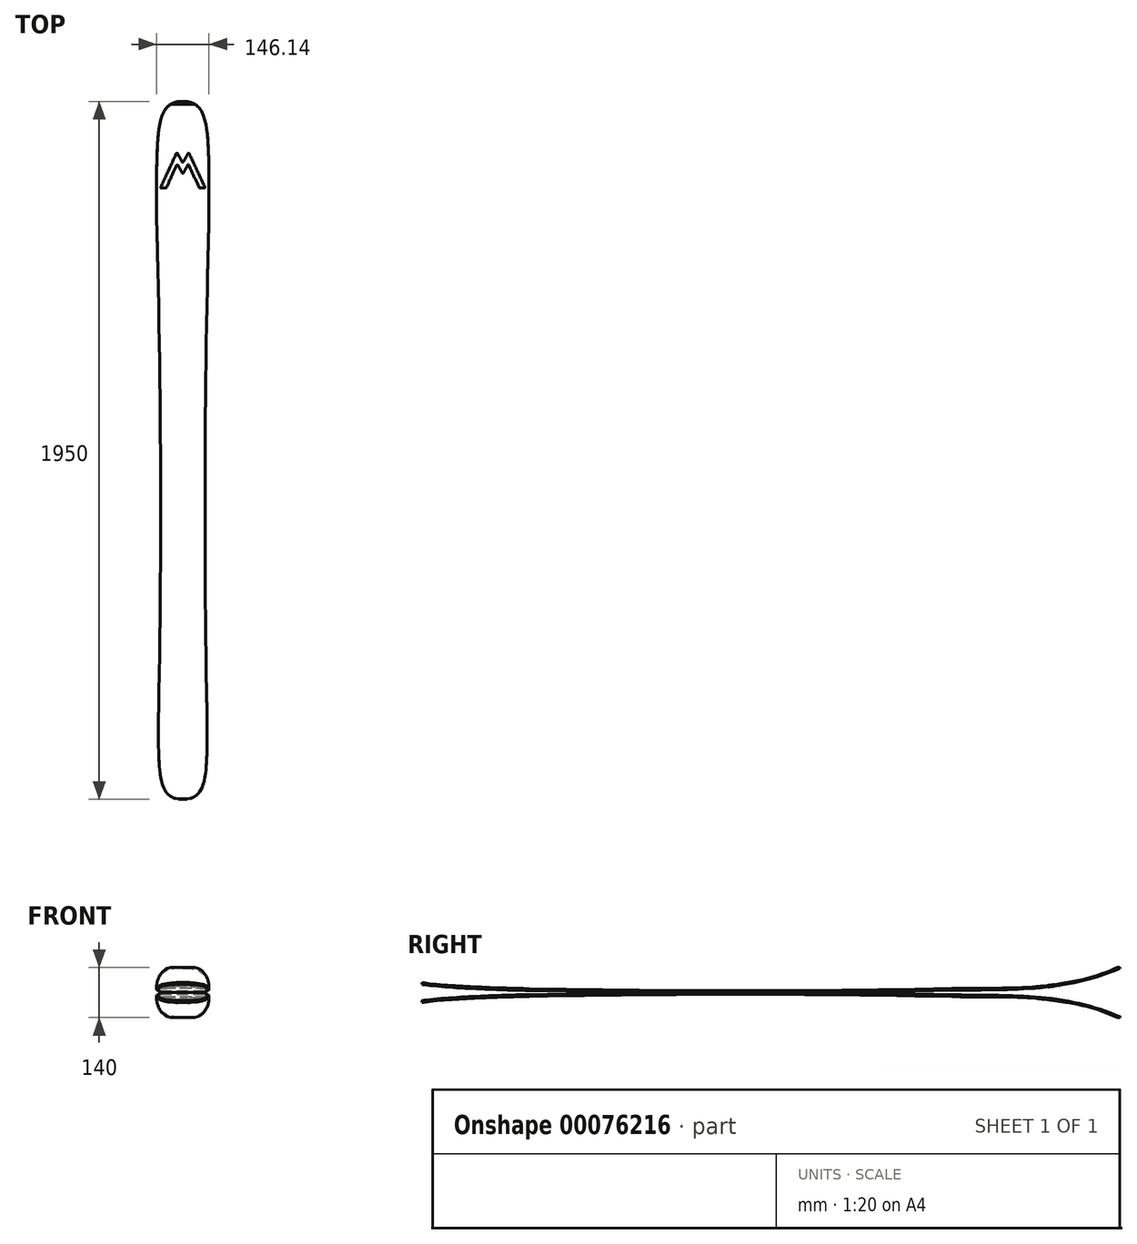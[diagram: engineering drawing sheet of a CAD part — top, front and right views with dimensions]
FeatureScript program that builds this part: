
annotation { "Feature Type Name" : "Feature", "Feature Type Description" : "" }
export const myFeature = defineFeature(function(context is Context, id is Id, definition is map)
    precondition{}
    {
        {
            var Q0;
            Q0=qCreatedBy(makeId("Right.planeOp"),FACE);
            var sketch = newSketch(context, id + "F0", { "sketchPlane" : qUnion([Q0])});
            skLineSegment(sketch, "E0", {"start": v(0, 23) * mm, "end": v(0, 0) * mm, "construction": true});
            skLineSegment(sketch, "E1", {"start": v(0, 0) * mm, "end": v(1950, 0) * mm, "construction": true});
            skLineSegment(sketch, "E2", {"start": v(1950, 0) * mm, "end": v(1950, 68) * mm, "construction": true});
            skLineSegment(sketch, "E3", {"start": v(880, 0) * mm, "end": v(880, 154.89) * mm, "construction": true});
            skLineSegment(sketch, "E4", {"start": v(300, 0) * mm, "end": v(300, 116.2) * mm, "construction": true});
            skLineSegment(sketch, "E5.MirrorCS", {"start": v(1480, 0) * mm, "end": v(1480, 116.2) * mm, "construction": true});
            skArc(sketch, "E6", {"start": v(300, 5.8) * mm, "mid": v(890, 0) * mm, "end": v(1480, 6.2) * mm});
            skFitSpline(sketch, "E7", {"points": [v(1480, 6.2) * mm, v(1950, 68) * mm], "startDerivative": vector(530.97, 10.99) * mm, "endDerivative": vector(480, 204) * mm});
            skFitSpline(sketch, "E8", {"points": [v(0, 23) * mm, v(300, 5.8) * mm], "startDerivative": vector(164.4, -29.03) * mm, "endDerivative": vector(280.54, -5.61) * mm});
            skFitSpline(sketch, "E9.0", {"points": [v(1479.9, 11.2) * mm, v(1524.2, 12.12) * mm, v(1607.23, 12.26) * mm, v(1702.48, 15.35) * mm, v(1776.9, 23.8) * mm, v(1851.28, 37.66) * mm, v(1908.31, 55.72) * mm, v(1948.04, 72.6) * mm]});
            skArc(sketch, "E9.1", {"start": v(300.1, 10.8) * mm, "mid": v(890, 5) * mm, "end": v(1479.9, 11.2) * mm});
            skFitSpline(sketch, "E9.2", {"points": [v(0.87, 27.92) * mm, v(4.22, 27.33) * mm, v(11.7, 26.17) * mm, v(29.49, 23.96) * mm, v(56.34, 21.42) * mm, v(94.05, 18.73) * mm, v(135.43, 16.4) * mm, v(178.64, 14.45) * mm, v(236.25, 12.32) * mm, v(276.74, 11.27) * mm, v(300.1, 10.8) * mm]});
            skLineSegment(sketch, "E10", {"start": v(0.87, 27.92) * mm, "end": v(0, 23) * mm});
            skLineSegment(sketch, "E11", {"start": v(1947.68, 72.45) * mm, "end": v(1950, 68) * mm});
            skSolve(sketch);
        }
        {
            var Q0;
            Q0=qCreatedBy(makeId("Top.planeOp"),FACE);
            var sketch = newSketch(context, id + "F1", { "sketchPlane" : qUnion([Q0])});
            skLineSegment(sketch, "E12", {"start": v(0, 0) * mm, "end": v(0, 1950) * mm, "construction": true});
            skLineSegment(sketch, "E13", {"start": v(0, 220) * mm, "end": v(-68, 220) * mm, "construction": true});
            skLineSegment(sketch, "E14", {"start": v(0, 0) * mm, "end": v(160.97, 0) * mm, "construction": true});
            skLineSegment(sketch, "E15", {"start": v(0, 1950) * mm, "end": v(182.14, 1950) * mm, "construction": true});
            skFitSpline(sketch, "E16", {"points": [v(0, 0) * mm, v(-68, 220) * mm], "startDerivative": vector(-204, 0) * mm, "endDerivative": vector(0, 475.06) * mm});
            skLineSegment(sketch, "E17", {"start": v(-68, 220) * mm, "end": v(-68, -176.43) * mm, "construction": true});
            skLineSegment(sketch, "E18", {"start": v(-73, 1615.04) * mm, "end": v(-73, 2125.31) * mm, "construction": true});
            skFitSpline(sketch, "E19", {"points": [v(-73, 1615.04) * mm, v(0, 1950) * mm], "startDerivative": vector(0, 765.41) * mm, "endDerivative": vector(234.67, 0) * mm});
            skLineSegment(sketch, "E20", {"start": v(0, 880) * mm, "end": v(-62, 880) * mm, "construction": true});
            skArc(sketch, "E21", {"start": v(-68, 220) * mm, "mid": v(-62.08, 907.74) * mm, "end": v(-72.46, 1595.42) * mm});
            skFitSpline(sketch, "E22.MirrorCS", {"points": [v(73, 1615.04) * mm, v(0, 1950) * mm], "startDerivative": vector(0, 765.41) * mm, "endDerivative": vector(-234.67, 0) * mm});
            skArc(sketch, "E23.MirrorCS", {"start": v(68, 220) * mm, "mid": v(62.08, 907.74) * mm, "end": v(72.46, 1595.42) * mm});
            skFitSpline(sketch, "E24.MirrorCS", {"points": [v(0, 0) * mm, v(68, 220) * mm], "startDerivative": vector(204, 0) * mm, "endDerivative": vector(0, 475.06) * mm});
            skLineSegment(sketch, "E25", {"start": v(364.28, 880) * mm, "end": v(-299.72, 880) * mm, "construction": true});
            skLineSegment(sketch, "E26", {"start": v(-73.07, 1707.71) * mm, "end": v(73.07, 1707.71) * mm, "construction": true});
            skLineSegment(sketch, "E27", {"start": v(63.07, 1707.71) * mm, "end": v(63.07, 1807.71) * mm, "construction": true});
            skLineSegment(sketch, "E28", {"start": v(63.07, 1807.71) * mm, "end": v(-105.68, 1807.71) * mm, "construction": true});
            skLineSegment(sketch, "E29", {"start": v(1.75, 1781.25) * mm, "end": v(14.55, 1804.29) * mm});
            skLineSegment(sketch, "E30", {"start": v(18.1, 1804.16) * mm, "end": v(61.74, 1710.56) * mm});
            skLineSegment(sketch, "E31.MirrorCS", {"start": v(-18.1, 1804.16) * mm, "end": v(-61.74, 1710.56) * mm});
            skLineSegment(sketch, "E32.MirrorCS", {"start": v(-1.75, 1781.25) * mm, "end": v(-14.55, 1804.29) * mm});
            skLineSegment(sketch, "E33.0", {"start": v(15.28, 1774.72) * mm, "end": v(45.98, 1708.87) * mm});
            skLineSegment(sketch, "E33.1", {"start": v(1.75, 1750.37) * mm, "end": v(15.28, 1774.72) * mm});
            skLineSegment(sketch, "E33.2", {"start": v(-1.75, 1750.37) * mm, "end": v(-13.38, 1771.3) * mm});
            skLineSegment(sketch, "E33.3", {"start": v(-16.94, 1771.17) * mm, "end": v(-45.98, 1708.87) * mm});
            skLineSegment(sketch, "E34", {"start": v(59.93, 1707.71) * mm, "end": v(47.8, 1707.71) * mm});
            skLineSegment(sketch, "E35", {"start": v(-59.93, 1707.71) * mm, "end": v(-47.8, 1707.71) * mm});
            skPoint(sketch, "E36.visualSharp", {"position": v(-46.52, 1707.71) * mm});
            skArc(sketch, "E36.filletArc", {"start": v(-47.8, 1707.71) * mm, "mid": v(-46.72, 1708.03) * mm, "end": v(-45.98, 1708.87) * mm});
            skPoint(sketch, "E37.visualSharp", {"position": v(-63.07, 1707.71) * mm});
            skArc(sketch, "E37.filletArc", {"start": v(-61.74, 1710.56) * mm, "mid": v(-61.62, 1708.64) * mm, "end": v(-59.93, 1707.71) * mm});
            skPoint(sketch, "E38.visualSharp", {"position": v(-16.45, 1807.71) * mm});
            skArc(sketch, "E38.filletArc", {"start": v(-14.55, 1804.29) * mm, "mid": v(-16.37, 1805.31) * mm, "end": v(-18.1, 1804.16) * mm});
            skPoint(sketch, "E39.visualSharp", {"position": v(-15.28, 1774.72) * mm});
            skArc(sketch, "E39.filletArc", {"start": v(-13.38, 1771.3) * mm, "mid": v(-15.2, 1772.32) * mm, "end": v(-16.94, 1771.17) * mm});
            skPoint(sketch, "E40.visualSharp", {"position": v(0, 1747.23) * mm});
            skArc(sketch, "E40.filletArc", {"start": v(-1.75, 1750.37) * mm, "mid": v(0, 1749.34) * mm, "end": v(1.75, 1750.37) * mm});
            skPoint(sketch, "E41.visualSharp", {"position": v(0, 1778.1) * mm});
            skArc(sketch, "E41.filletArc", {"start": v(-1.75, 1781.25) * mm, "mid": v(0, 1780.23) * mm, "end": v(1.75, 1781.25) * mm});
            skPoint(sketch, "E42.visualSharp", {"position": v(16.45, 1807.71) * mm});
            skArc(sketch, "E42.filletArc", {"start": v(18.1, 1804.16) * mm, "mid": v(16.37, 1805.31) * mm, "end": v(14.55, 1804.29) * mm});
            skPoint(sketch, "E43.visualSharp", {"position": v(63.07, 1707.71) * mm});
            skArc(sketch, "E43.filletArc", {"start": v(59.93, 1707.71) * mm, "mid": v(61.62, 1708.64) * mm, "end": v(61.74, 1710.56) * mm});
            skPoint(sketch, "E44.visualSharp", {"position": v(46.52, 1707.71) * mm});
            skArc(sketch, "E44.filletArc", {"start": v(45.98, 1708.87) * mm, "mid": v(46.72, 1708.03) * mm, "end": v(47.8, 1707.71) * mm});
            skArc(sketch, "E45.0.filletArc", {"start": v(72.46, 1595.42) * mm, "mid": v(72.86, 1615) * mm, "end": v(73, 1634.57) * mm});
            skArc(sketch, "E46.0.filletArc", {"start": v(-73, 1634.57) * mm, "mid": v(-72.86, 1615) * mm, "end": v(-72.46, 1595.42) * mm});
            skSolve(sketch);
        }
        {
            var Q0;
            Q0 = qSketchRegion(id + "F1", true);
            extrude(context, id + "F2", {"entities" : qUnion([Q0]), "depth" : 70 * mm});
        }
        {
            var Q0;
            Q0 = qSketchRegion(id + "F0", true);
            extrude(context, id + "F3", {"entities" : qUnion([Q0]), "operationType" : NewBodyOperationType.INTERSECT, "oppositeDirection" : true, "depth" : 160 * mm, "symmetric" : true});
        }
        {
            var Q0;
            Q0=makeQuery(id+"F2.opExtrude","SWEPT_BODY",BODY,{"disambiguationData":[OSD([sQuery(id+"F1.wireOp",EDGE,"E16"),sQuery(id+"F1.wireOp",EDGE,"E19"),sQuery(id+"F1.wireOp",EDGE,"E21"),sQuery(id+"F1.wireOp",EDGE,"E22.MirrorCS"),sQuery(id+"F1.wireOp",EDGE,"E23.MirrorCS"),sQuery(id+"F1.wireOp",EDGE,"E24.MirrorCS"),sQuery(id+"F1.wireOp",EDGE,"E29"),sQuery(id+"F1.wireOp",EDGE,"E30"),sQuery(id+"F1.wireOp",EDGE,"E31.MirrorCS"),sQuery(id+"F1.wireOp",EDGE,"E32.MirrorCS"),sQuery(id+"F1.wireOp",EDGE,"E33.0"),sQuery(id+"F1.wireOp",EDGE,"E33.1"),sQuery(id+"F1.wireOp",EDGE,"E33.2"),sQuery(id+"F1.wireOp",EDGE,"E33.3"),sQuery(id+"F1.wireOp",EDGE,"E34"),sQuery(id+"F1.wireOp",EDGE,"E35"),sQuery(id+"F1.wireOp",EDGE,"E36.filletArc"),sQuery(id+"F1.wireOp",EDGE,"E37.filletArc"),sQuery(id+"F1.wireOp",EDGE,"E38.filletArc"),sQuery(id+"F1.wireOp",EDGE,"E39.filletArc"),sQuery(id+"F1.wireOp",EDGE,"E40.filletArc"),sQuery(id+"F1.wireOp",EDGE,"E41.filletArc"),sQuery(id+"F1.wireOp",EDGE,"E42.filletArc"),sQuery(id+"F1.wireOp",EDGE,"E43.filletArc"),sQuery(id+"F1.wireOp",EDGE,"E44.filletArc")])]});
            var Q1;
            Q1=qCreatedBy(makeId("Top.planeOp"),FACE);
            mirror(context, id + "F4", {"operationType" : NewBodyOperationType.ADD, "entities" : qUnion([Q0]), "mirrorPlane" : qUnion([Q1])});
        }
    });
